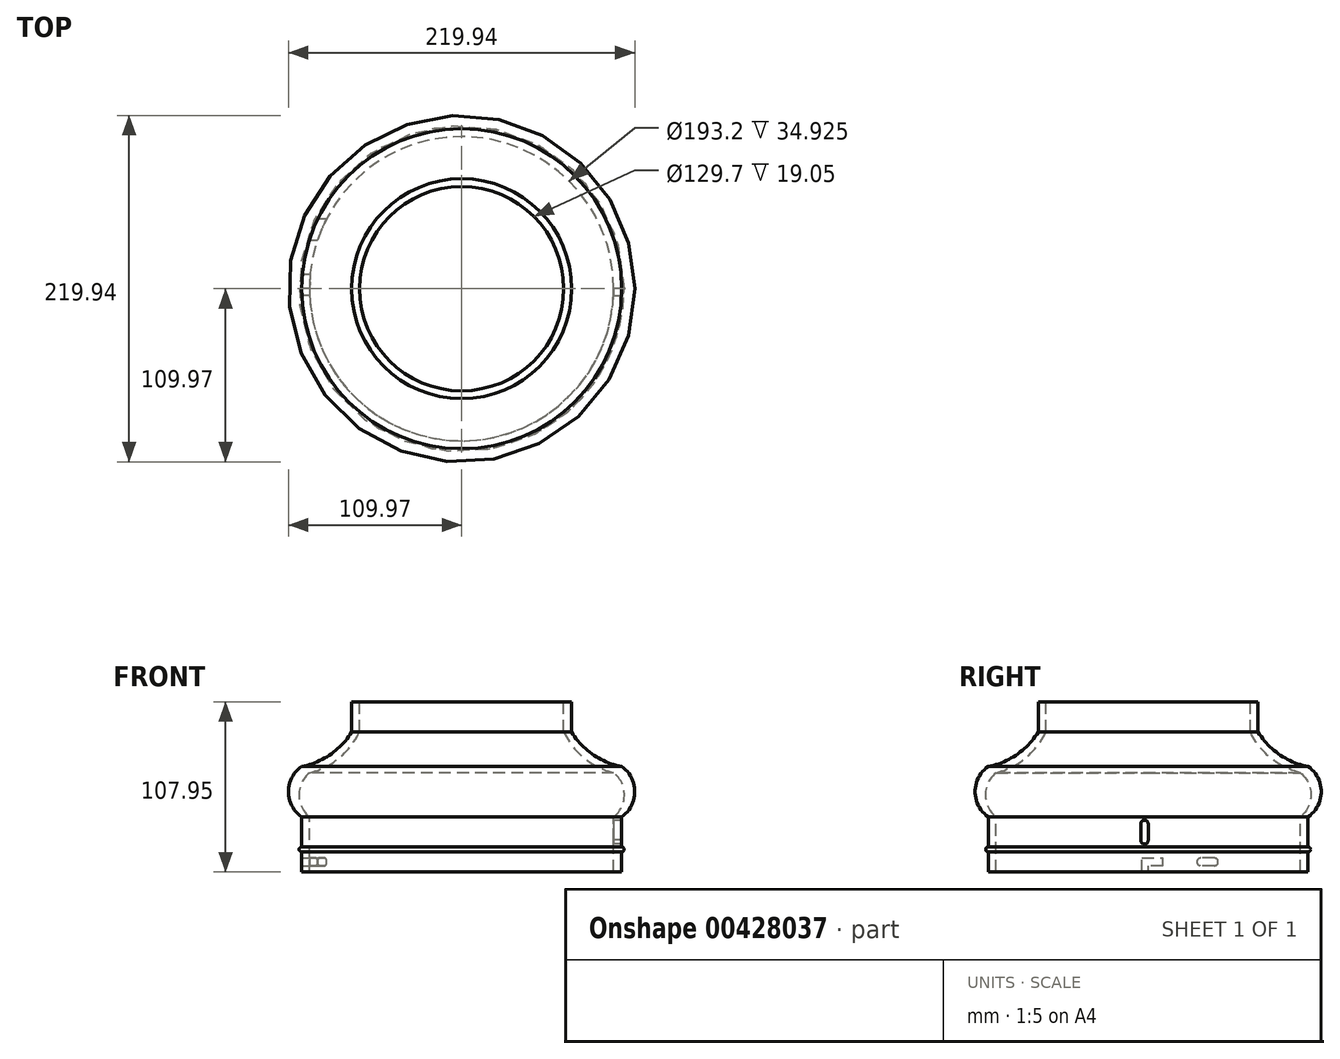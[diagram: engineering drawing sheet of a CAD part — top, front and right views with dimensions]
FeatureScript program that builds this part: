
annotation { "Feature Type Name" : "Feature", "Feature Type Description" : "" }
export const myFeature = defineFeature(function(context is Context, id is Id, definition is map)
    precondition{}
    {
        {
            var Q0;
            Q0=qCreatedBy(makeId("Front.planeOp"),FACE);
            var sketch = newSketch(context, id + "F0", { "sketchPlane" : qUnion([Q0])});
            skLineSegment(sketch, "E0.bottom", {"start": v(101.6, -107.95) * mm, "end": v(101.6, -107.95) * mm});
            skLineSegment(sketch, "E0.top", {"start": v(101.6, -95.25) * mm, "end": v(101.6, -95.25) * mm});
            skLineSegment(sketch, "E0.left", {"start": v(101.6, -107.95) * mm, "end": v(101.6, -95.25) * mm});
            skLineSegment(sketch, "E0.right", {"start": v(101.6, -107.95) * mm, "end": v(101.6, -95.25) * mm});
            skArc(sketch, "E1", {"start": v(101.6, -95.25) * mm, "mid": v(103.19, -93.66) * mm, "end": v(101.6, -92.08) * mm});
            skLineSegment(sketch, "E2", {"start": v(101.6, -92.08) * mm, "end": v(101.6, -73.03) * mm});
            skLineSegment(sketch, "E3", {"start": v(69.85, 0) * mm, "end": v(69.85, -19.05) * mm});
            skArc(sketch, "E4", {"start": v(101.6, -73.03) * mm, "mid": v(109.97, -56.99) * mm, "end": v(101.6, -40.95) * mm});
            skArc(sketch, "E5", {"start": v(69.85, -19.05) * mm, "mid": v(83.39, -33.4) * mm, "end": v(101.6, -40.95) * mm});
            skLineSegment(sketch, "E6", {"start": v(69.85, 0) * mm, "end": v(64.85, 0) * mm});
            skLineSegment(sketch, "E7", {"start": v(64.85, 0) * mm, "end": v(64.85, -19.05) * mm});
            skLineSegment(sketch, "E8", {"start": v(101.6, -107.95) * mm, "end": v(96.6, -107.95) * mm});
            skLineSegment(sketch, "E9", {"start": v(96.6, -107.95) * mm, "end": v(96.6, -73.03) * mm});
            skPoint(sketch, "E10", {"position": v(96.6, -44.94) * mm});
            skArc(sketch, "E11", {"start": v(64.85, -19.05) * mm, "mid": v(77.78, -35.6) * mm, "end": v(96.6, -44.94) * mm});
            skArc(sketch, "E12", {"start": v(96.6, -73.03) * mm, "mid": v(103.36, -58.98) * mm, "end": v(96.6, -44.94) * mm});
            skSolve(sketch);
        }
        {
            var Q0;
            Q0=qCreatedBy(makeId("Front.planeOp"),FACE);
            var sketch = newSketch(context, id + "F1", { "sketchPlane" : qUnion([Q0])});
            skLineSegment(sketch, "E13", {"start": v(0, -1.96) * mm, "end": v(0, -72.7) * mm});
            skSolve(sketch);
        }
        {
            var Q0;
            Q0 = qSketchRegion(id + "F0", true);
            var Q1;
            Q1=sQuery(id+"F1.wireOp",EDGE,"E13");
            revolve(context, id + "F2", {"entities" : qUnion([Q0]), "axis" : qUnion([Q1]), "revolveType" : RevolveType.FULL});
        }
        {
            var Q0;
            Q0=qCreatedBy(makeId("Right.planeOp"),FACE);
            var sketch = newSketch(context, id + "F3", { "sketchPlane" : qUnion([Q0])});
            skLineSegment(sketch, "E14", {"start": v(0, -77.44) * mm, "end": v(0, -87.66) * mm});
            skLineSegment(sketch, "E15", {"start": v(0, -77.44) * mm, "end": v(-4.73, -77.44) * mm});
            skLineSegment(sketch, "E16", {"start": v(-4.73, -87.89) * mm, "end": v(0, -87.66) * mm});
            skLineSegment(sketch, "E17", {"start": v(-4.73, -77.44) * mm, "end": v(-4.73, -87.89) * mm});
            skArc(sketch, "E18", {"start": v(-4.73, -87.89) * mm, "mid": v(-2.25, -90.25) * mm, "end": v(0, -87.66) * mm});
            skArc(sketch, "E19", {"start": v(0, -77.44) * mm, "mid": v(-2.36, -75.07) * mm, "end": v(-4.73, -77.44) * mm});
            skSolve(sketch);
        }
        {
            var Q0;
            Q0 = qSketchRegion(id + "F3", true);
            extrude(context, id + "F4", {"entities" : qUnion([Q0]), "operationType" : NewBodyOperationType.REMOVE, "depth" : 2540 * mm});
        }
        {
            var Q0;
            Q0=qCreatedBy(makeId("Right.planeOp"),FACE);
            var sketch = newSketch(context, id + "F5", { "sketchPlane" : qUnion([Q0])});
            skLineSegment(sketch, "E20.bottom", {"start": v(42.01, -99.17) * mm, "end": v(33.4, -99.17) * mm});
            skLineSegment(sketch, "E20.top", {"start": v(42.01, -104.03) * mm, "end": v(33.4, -104.03) * mm});
            skLineSegment(sketch, "E20.left", {"start": v(42.01, -99.17) * mm, "end": v(42.01, -104.03) * mm});
            skLineSegment(sketch, "E20.right", {"start": v(33.4, -99.17) * mm, "end": v(33.4, -104.03) * mm});
            skArc(sketch, "E21", {"start": v(33.4, -99.17) * mm, "mid": v(30.96, -101.6) * mm, "end": v(33.4, -104.03) * mm});
            skArc(sketch, "E22", {"start": v(42.01, -104.03) * mm, "mid": v(44.45, -101.6) * mm, "end": v(42.01, -99.17) * mm});
            skLineSegment(sketch, "E23.bottom", {"start": v(0, -107.97) * mm, "end": v(0, -107.97) * mm});
            skLineSegment(sketch, "E24.bottom", {"start": v(0, -106.15) * mm, "end": v(0, -106.15) * mm});
            skLineSegment(sketch, "E25.bottom", {"start": v(-2.16, -103.35) * mm, "end": v(-1.97, -103.35) * mm});
            skLineSegment(sketch, "E25.top", {"start": v(-2.16, -107.95) * mm, "end": v(-1.97, -107.95) * mm});
            skLineSegment(sketch, "E26", {"start": v(-1.97, -99.17) * mm, "end": v(9.35, -99.17) * mm});
            skLineSegment(sketch, "E27", {"start": v(9.35, -99.17) * mm, "end": v(9.35, -103.35) * mm});
            skLineSegment(sketch, "E28", {"start": v(9.35, -99.17) * mm, "end": v(9.35, -104.03) * mm});
            skLineSegment(sketch, "E29", {"start": v(-1.97, -99.17) * mm, "end": v(-3.88, -99.17) * mm});
            skLineSegment(sketch, "E30", {"start": v(-3.88, -99.17) * mm, "end": v(-3.88, -107.95) * mm});
            skLineSegment(sketch, "E31", {"start": v(9.35, -104.03) * mm, "end": v(0, -104.03) * mm});
            skLineSegment(sketch, "E32", {"start": v(0, -104.03) * mm, "end": v(0, -107.97) * mm});
            skLineSegment(sketch, "E33", {"start": v(0, -107.97) * mm, "end": v(-3.88, -107.95) * mm});
            skSolve(sketch);
        }
        {
            var Q0;
            Q0 = qSketchRegion(id + "F5", true);
            extrude(context, id + "F6", {"entities" : qUnion([Q0]), "operationType" : NewBodyOperationType.REMOVE, "oppositeDirection" : true, "depth" : 2540 * mm});
        }
    });
